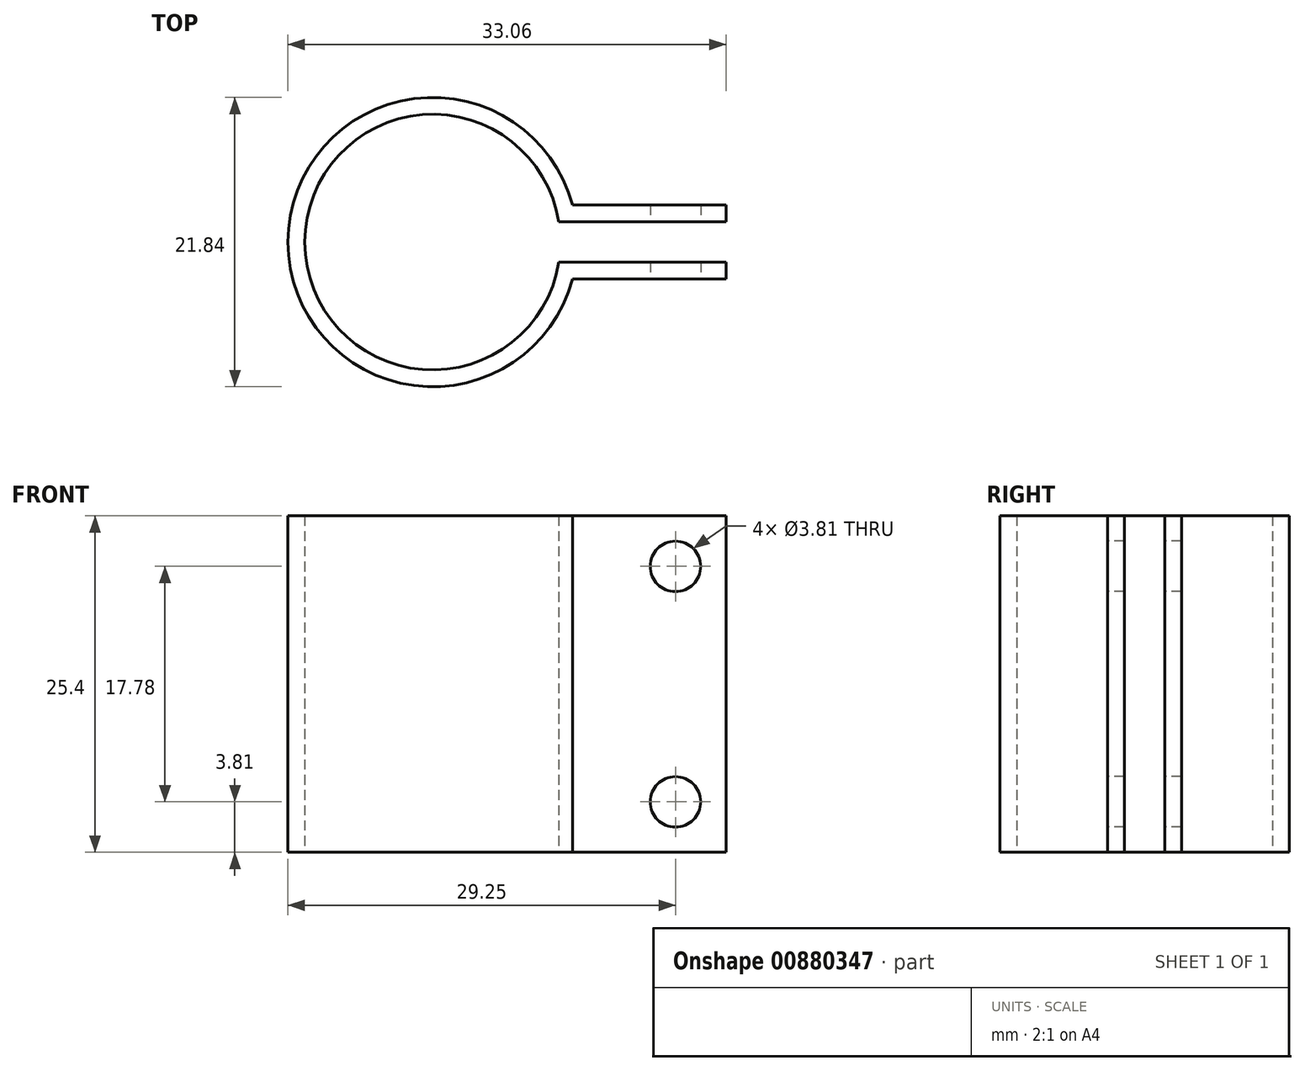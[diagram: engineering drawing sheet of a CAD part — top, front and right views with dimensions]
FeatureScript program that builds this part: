
annotation { "Feature Type Name" : "Feature", "Feature Type Description" : "" }
export const myFeature = defineFeature(function(context is Context, id is Id, definition is map)
    precondition{}
    {
        {
            var Q0;
            Q0=qCreatedBy(makeId("Top.planeOp"),FACE);
            var sketch = newSketch(context, id + "F0", { "sketchPlane" : qUnion([Q0])});
            skArc(sketch, "E0", {"start": v(6.44, 1.52) * mm, "mid": v(-12.74, 0) * mm, "end": v(6.44, -1.52) * mm});
            skArc(sketch, "E1", {"start": v(7.47, 2.8) * mm, "mid": v(-14.01, 0) * mm, "end": v(7.47, -2.8) * mm});
            skLineSegment(sketch, "E2.bottom", {"start": v(19.05, -1.52) * mm, "end": v(6.44, -1.52) * mm});
            skLineSegment(sketch, "E2.top", {"start": v(19.05, 1.52) * mm, "end": v(6.44, 1.52) * mm});
            skPoint(sketch, "E2.middle", {"position": v(0, 0) * mm});
            skPoint(sketch, "E2.right.end.orphan", {"position": v(-19.05, 1.52) * mm});
            skPoint(sketch, "E3.orphan", {"position": v(-19.05, -1.52) * mm});
            skLineSegment(sketch, "E4.0", {"start": v(19.05, 2.8) * mm, "end": v(7.47, 2.8) * mm});
            skLineSegment(sketch, "E5.0", {"start": v(19.05, -2.8) * mm, "end": v(7.47, -2.8) * mm});
            skLineSegment(sketch, "E6", {"start": v(19.05, 2.8) * mm, "end": v(19.05, 1.52) * mm});
            skLineSegment(sketch, "E7", {"start": v(19.05, -1.52) * mm, "end": v(19.05, -2.8) * mm});
            skSolve(sketch);
        }
        {
            var Q0;
            Q0 = qSketchRegion(id + "F0", true);
            extrude(context, id + "F1", {"entities" : qUnion([Q0]), "depth" : 25.4 * mm, "offsetDistance" : 25.4 * mm});
        }
        {
            var Q0;
            Q0=makeQuery(id+"F1.opExtrude","SWEPT_FACE",FACE,{"disambiguationData":[OSD([sQuery(id+"F0.wireOp",EDGE,"E5.0")])]});
            var sketch = newSketch(context, id + "F2", { "sketchPlane" : qUnion([Q0])});
            skCircle(sketch, "E8", {"center": v(15.24, 21.59) * mm, "radius": 1.9 * mm});
            skCircle(sketch, "E9", {"center": v(15.24, 3.81) * mm, "radius": 1.9 * mm});
            skSolve(sketch);
        }
        {
            var Q0;
            Q0 = qSketchRegion(id + "F2", true);
            extrude(context, id + "F3", {"entities" : qUnion([Q0]), "operationType" : NewBodyOperationType.REMOVE, "oppositeDirection" : true, "depth" : 25.4 * mm, "offsetDistance" : 25.4 * mm});
        }
    });
